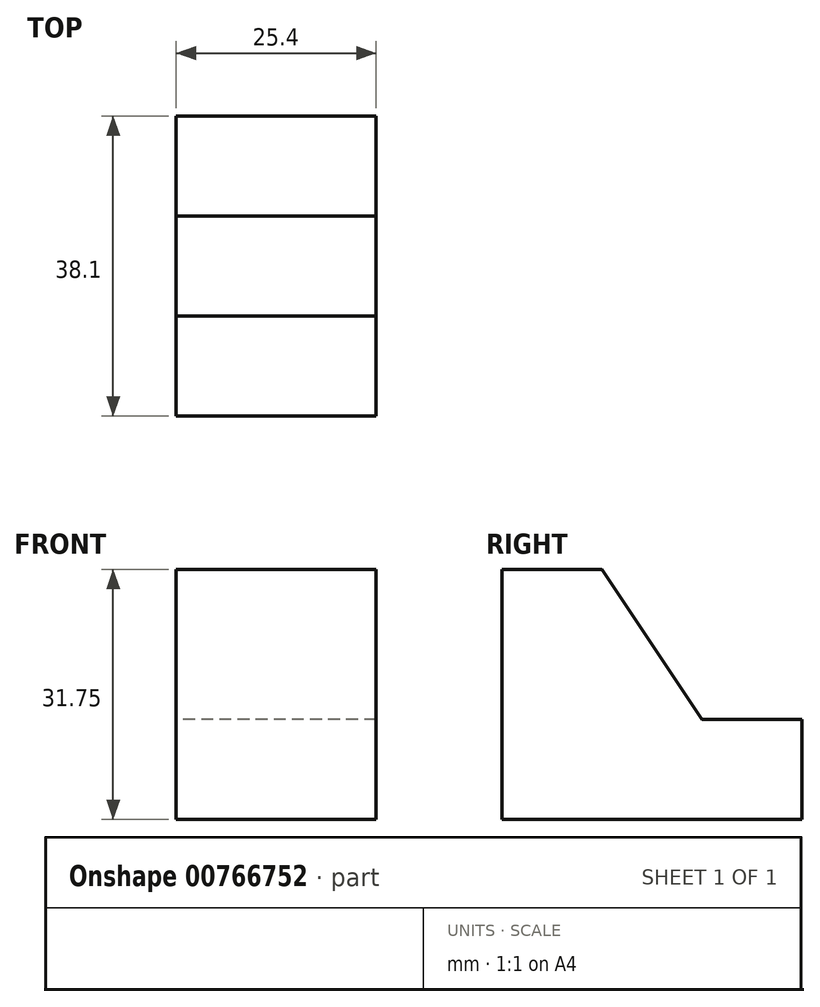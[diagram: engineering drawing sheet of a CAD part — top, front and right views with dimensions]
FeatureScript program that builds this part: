
annotation { "Feature Type Name" : "Feature", "Feature Type Description" : "" }
export const myFeature = defineFeature(function(context is Context, id is Id, definition is map)
    precondition{}
    {
        {
            var Q0;
            Q0=qCreatedBy(makeId("Right.planeOp"),FACE);
            var sketch = newSketch(context, id + "F0", { "sketchPlane" : qUnion([Q0])});
            skLineSegment(sketch, "E0", {"start": v(0, 0) * mm, "end": v(0, 31.75) * mm});
            skLineSegment(sketch, "E1", {"start": v(0, 31.75) * mm, "end": v(12.7, 31.75) * mm});
            skLineSegment(sketch, "E2", {"start": v(0, 0) * mm, "end": v(38.1, 0) * mm});
            skLineSegment(sketch, "E3", {"start": v(38.1, 0) * mm, "end": v(38.1, 12.7) * mm});
            skLineSegment(sketch, "E4", {"start": v(38.1, 12.7) * mm, "end": v(25.4, 12.7) * mm});
            skLineSegment(sketch, "E5", {"start": v(12.7, 31.75) * mm, "end": v(25.4, 12.7) * mm});
            skSolve(sketch);
        }
        {
            var Q0;
            Q0 = qSketchRegion(id + "F0", true);
            extrude(context, id + "F1", {"entities" : qUnion([Q0]), "depth" : 25.4 * mm, "offsetDistance" : 25.4 * mm});
        }
    });
